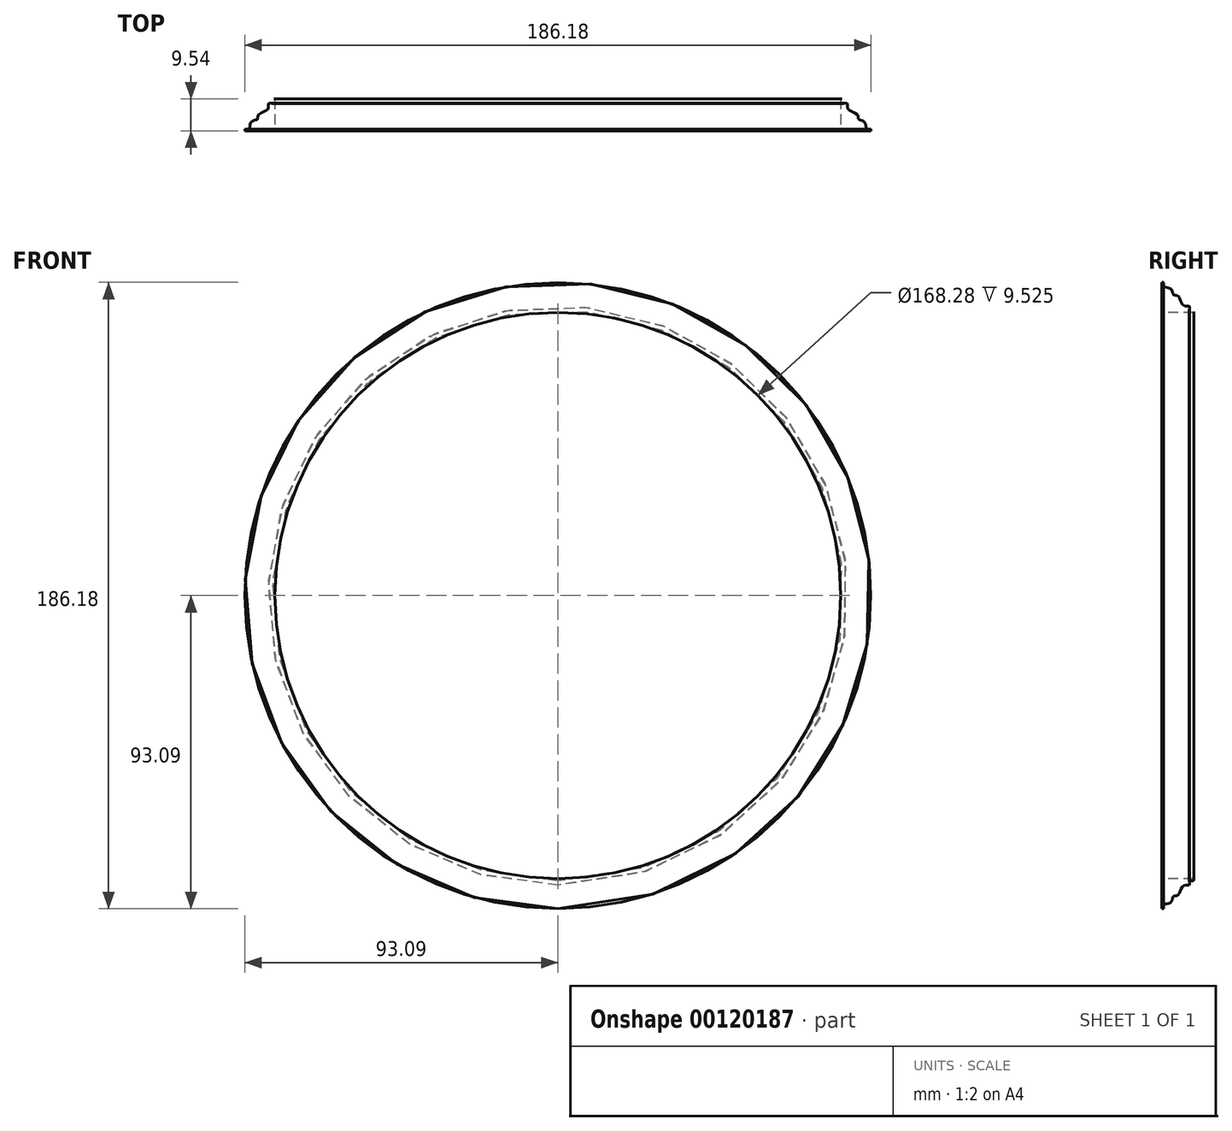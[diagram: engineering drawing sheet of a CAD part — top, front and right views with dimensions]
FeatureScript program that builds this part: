
annotation { "Feature Type Name" : "Feature", "Feature Type Description" : "" }
export const myFeature = defineFeature(function(context is Context, id is Id, definition is map)
    precondition{}
    {
        {
            var Q0;
            Q0=qCreatedBy(makeId("Right.planeOp"),FACE);
            var sketch = newSketch(context, id + "F0", { "sketchPlane" : qUnion([Q0])});
            skLineSegment(sketch, "E0", {"start": v(-29.38, 0) * mm, "end": v(31.15, 0) * mm});
            skLineSegment(sketch, "E1", {"start": v(0, 84.14) * mm, "end": v(9.53, 84.14) * mm});
            skLineSegment(sketch, "E2", {"start": v(0, 84.14) * mm, "end": v(0, 93.03) * mm});
            skFitSpline(sketch, "E3", {"points": [v(0, 93.03) * mm, v(0.5, 93.03) * mm, v(0.5, 92.21) * mm, v(0.84, 91.77) * mm, v(2.36, 91.36) * mm, v(3.17, 90.39) * mm, v(3.48, 89.4) * mm, v(4.84, 89) * mm, v(6.61, 86.18) * mm, v(8.25, 85.96) * mm, v(8.18, 84.8) * mm, v(9.36, 84.78) * mm, v(9.53, 84.14) * mm], "startDerivative": vector(11.61, 3.01) * mm, "endDerivative": vector(-1.26, -13.77) * mm});
            skSolve(sketch);
        }
        {
            var Q0;
            Q0 = qSketchRegion(id + "F0", true);
            var Q1;
            Q1=sQuery(id+"F0.wireOp",EDGE,"E0");
            revolve(context, id + "F1", {"entities" : qUnion([Q0]), "axis" : qUnion([Q1]), "revolveType" : RevolveType.FULL});
        }
    });
